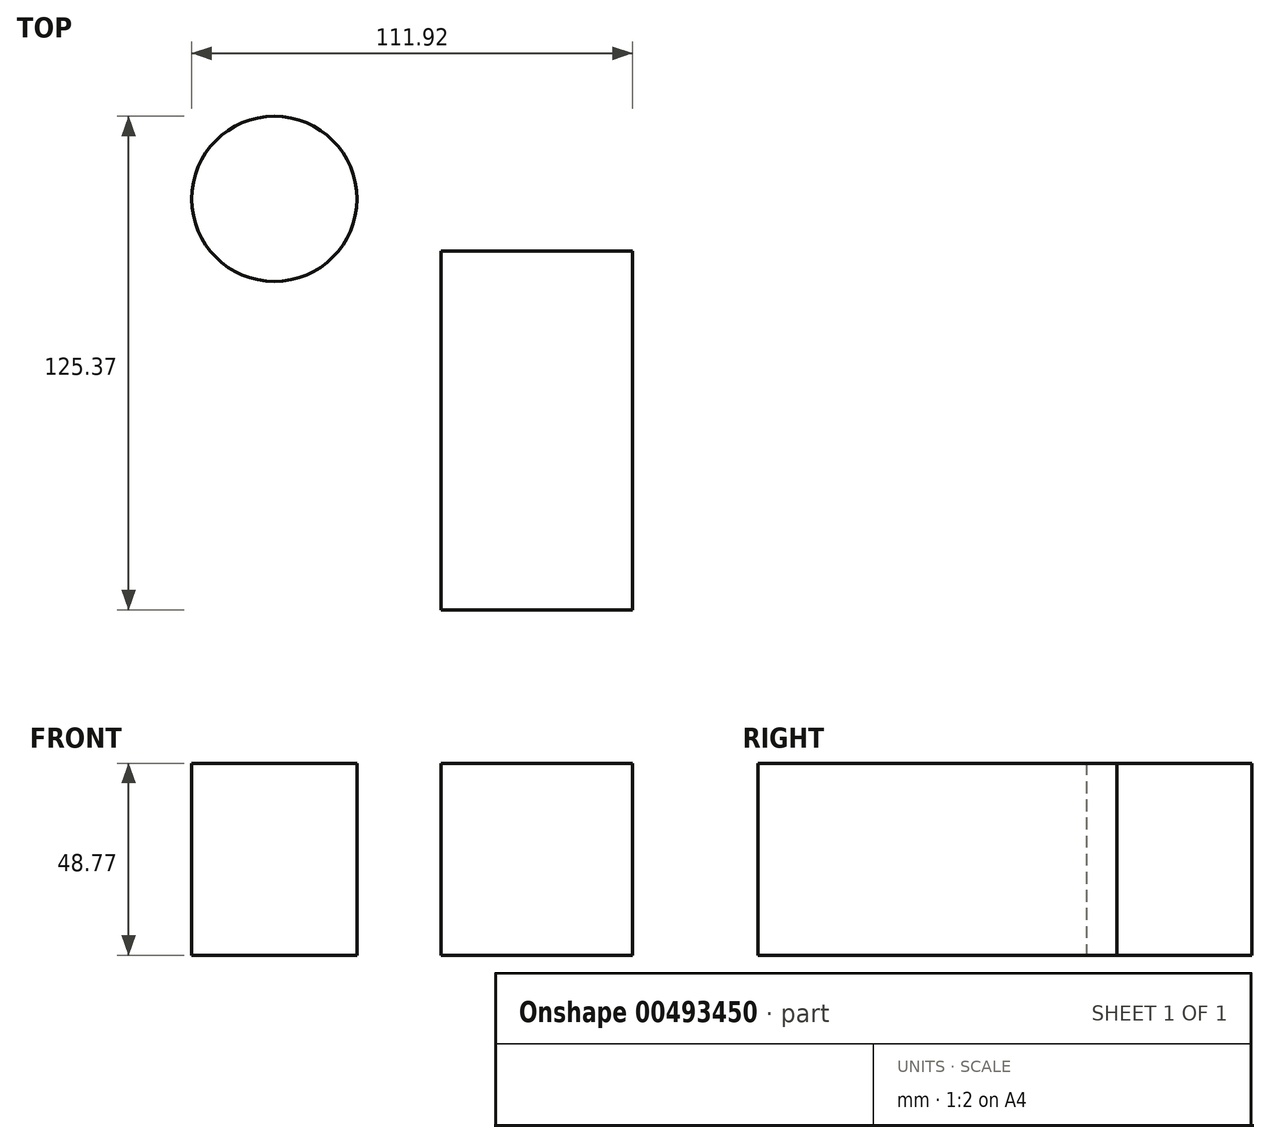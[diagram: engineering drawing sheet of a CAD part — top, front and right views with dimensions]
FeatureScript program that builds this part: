
annotation { "Feature Type Name" : "Feature", "Feature Type Description" : "" }
export const myFeature = defineFeature(function(context is Context, id is Id, definition is map)
    precondition{}
    {
        {
            var Q0;
            Q0=qCreatedBy(makeId("Top.planeOp"),FACE);
            var sketch = newSketch(context, id + "F0", { "sketchPlane" : qUnion([Q0])});
            skCircle(sketch, "E0", {"center": v(-145.21, 35.56) * mm, "radius": 21.36 * mm});
            skCircle(sketch, "E1", {"center": v(-145.21, 35.56) * mm, "radius": 20.99 * mm});
            skLineSegment(sketch, "E2.bottom", {"start": v(-102.87, 22.32) * mm, "end": v(-54.28, 22.32) * mm});
            skLineSegment(sketch, "E2.top", {"start": v(-102.87, -68.83) * mm, "end": v(-54.28, -68.83) * mm});
            skLineSegment(sketch, "E2.left", {"start": v(-102.87, 22.32) * mm, "end": v(-102.87, -68.83) * mm});
            skLineSegment(sketch, "E2.right", {"start": v(-54.28, 22.32) * mm, "end": v(-54.28, -68.83) * mm});
            skLineSegment(sketch, "E3.bottom", {"start": v(-54.28, -68.83) * mm, "end": v(-131.46, -68.83) * mm});
            skLineSegment(sketch, "E3.top", {"start": v(-54.28, -112.24) * mm, "end": v(-131.46, -112.24) * mm});
            skLineSegment(sketch, "E3.left", {"start": v(-54.28, -68.83) * mm, "end": v(-54.28, -112.24) * mm});
            skLineSegment(sketch, "E3.right", {"start": v(-131.46, -68.83) * mm, "end": v(-131.46, -112.24) * mm});
            skSolve(sketch);
        }
        {
            var Q0;
            Q0=makeQuery(id+"F0.imprint","IMPRINT",FACE,{"disambiguationData":[TD([[makeQuery(id+"F0.imprint","IMPRINT",EDGE,{"derivedFrom":sQuery(id+"F0.wireOp",EDGE,"E1")}),1.0]])]});
            var Q1;
            Q1=makeQuery(id+"F0.imprint","IMPRINT",FACE,{"disambiguationData":[TD([[makeQuery(id+"F0.imprint","IMPRINT",EDGE,{"derivedFrom":sQuery(id+"F0.wireOp",EDGE,"E2.bottom")}),-1.0]])]});
            extrude(context, id + "F1", {"entities" : qUnion([Q0, Q1]), "depth" : 48.77 * mm});
        }
    });
